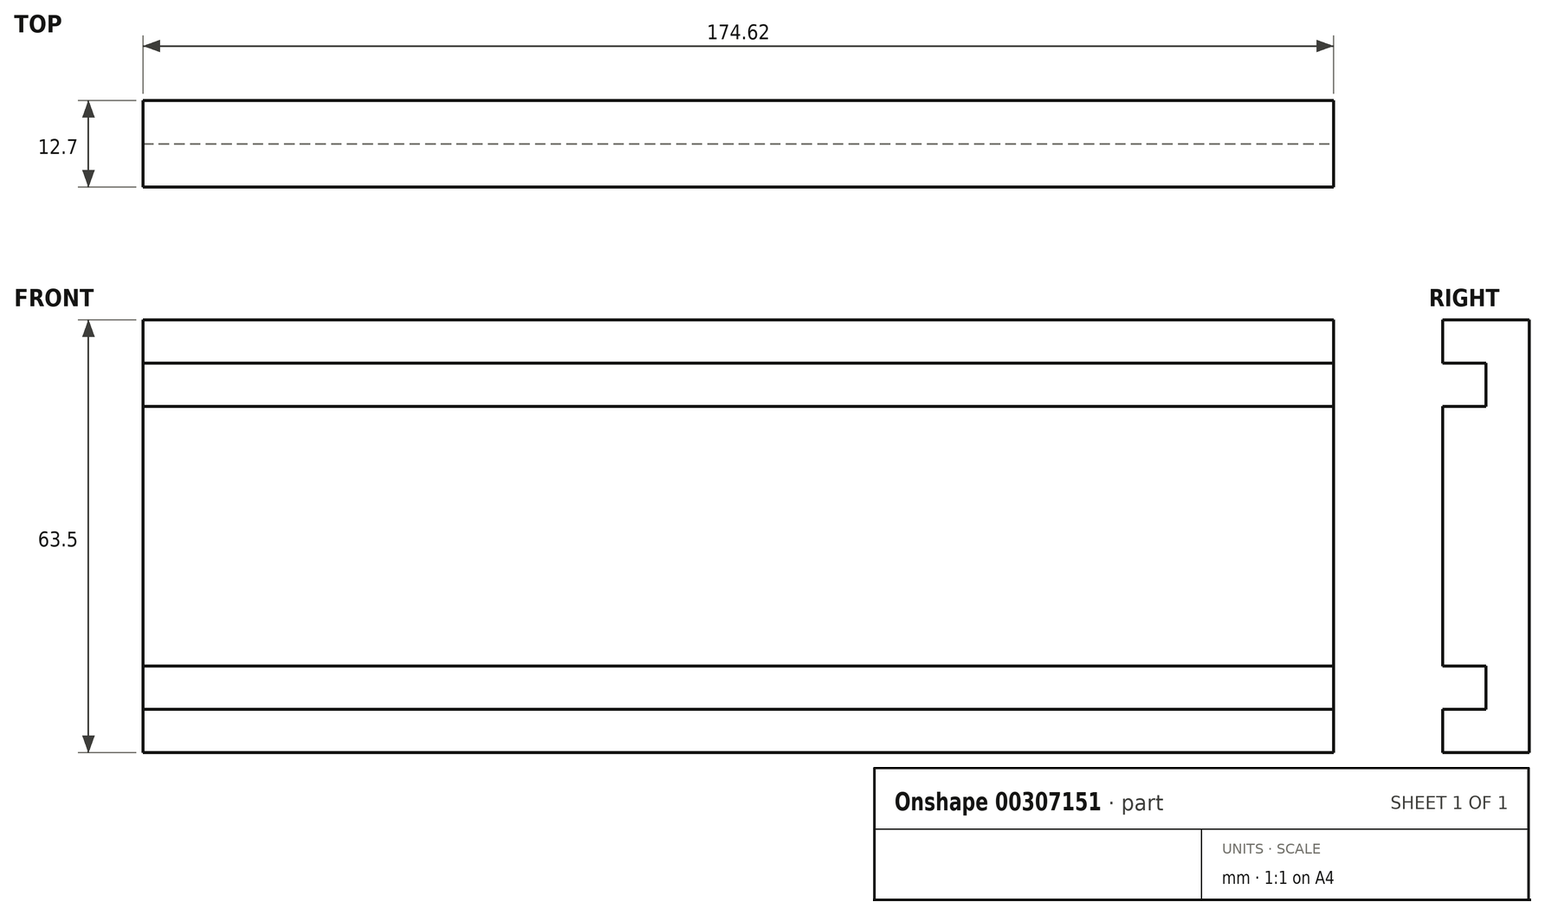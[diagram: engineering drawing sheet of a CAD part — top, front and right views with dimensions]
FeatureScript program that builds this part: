
annotation { "Feature Type Name" : "Feature", "Feature Type Description" : "" }
export const myFeature = defineFeature(function(context is Context, id is Id, definition is map)
    precondition{}
    {
        {
            var Q0;
            Q0=qCreatedBy(makeId("Front.planeOp"),FACE);
            var sketch = newSketch(context, id + "F0", { "sketchPlane" : qUnion([Q0])});
            skLineSegment(sketch, "E0.bottom", {"start": v(87.31, -31.75) * mm, "end": v(-87.31, -31.75) * mm});
            skLineSegment(sketch, "E0.top", {"start": v(87.31, 31.75) * mm, "end": v(-87.31, 31.75) * mm});
            skLineSegment(sketch, "E0.left", {"start": v(87.31, -31.75) * mm, "end": v(87.31, 31.75) * mm});
            skLineSegment(sketch, "E0.right", {"start": v(-87.31, -31.75) * mm, "end": v(-87.31, 31.75) * mm});
            skPoint(sketch, "E0.middle", {"position": v(0, 0) * mm});
            skSolve(sketch);
        }
        {
            var Q0;
            Q0=makeQuery(id+"F0.imprint","IMPRINT",FACE,{"disambiguationData":[TD([[makeQuery(id+"F0.imprint","IMPRINT",EDGE,{"derivedFrom":sQuery(id+"F0.wireOp",EDGE,"E0.bottom")}),-1.0]])]});
            extrude(context, id + "F1", {"entities" : qUnion([Q0]), "depth" : 12.7 * mm});
        }
        {
            var Q0;
            Q0=makeQuery(id+"F1.opExtrude","SWEPT_FACE",FACE,{"disambiguationData":[OSD([sQuery(id+"F0.wireOp",EDGE,"E0.left")])]});
            var sketch = newSketch(context, id + "F2", { "sketchPlane" : qUnion([Q0])});
            skLineSegment(sketch, "E1", {"start": v(-12.7, 25.4) * mm, "end": v(-6.35, 25.4) * mm});
            skLineSegment(sketch, "E2", {"start": v(-6.35, 25.4) * mm, "end": v(-6.35, 19.05) * mm});
            skLineSegment(sketch, "E3", {"start": v(-6.35, 19.05) * mm, "end": v(-12.7, 19.05) * mm});
            skLineSegment(sketch, "E4", {"start": v(-12.7, 19.05) * mm, "end": v(-12.7, -19.05) * mm});
            skLineSegment(sketch, "E5", {"start": v(-12.7, -19.05) * mm, "end": v(-6.35, -19.05) * mm});
            skLineSegment(sketch, "E6", {"start": v(-6.35, -19.05) * mm, "end": v(-6.35, -25.4) * mm});
            skLineSegment(sketch, "E7", {"start": v(-6.35, -25.4) * mm, "end": v(-12.7, -25.4) * mm});
            skSolve(sketch);
        }
        {
            var Q0;
            {var subQ0=sQuery(id+"F2.wireOp",EDGE,"E1");Q0=makeQuery(id+"F2.imprint","IMPRINT",FACE,{"disambiguationData":[TD([[makeQuery(id+"F2.imprint","IMPRINT",EDGE,{"derivedFrom":subQ0}),-1.0]])]});}
            var Q1;
            {var subQ0=sQuery(id+"F2.wireOp",EDGE,"E5");Q1=makeQuery(id+"F2.imprint","IMPRINT",FACE,{"disambiguationData":[TD([[makeQuery(id+"F2.imprint","IMPRINT",EDGE,{"derivedFrom":subQ0}),-1.0]])]});}
            var Q2;
            Q2=makeQuery(id+"F1.opExtrude","SWEPT_FACE",FACE,{"disambiguationData":[OSD([sQuery(id+"F0.wireOp",EDGE,"E0.right")])]});
            extrude(context, id + "F3", {"entities" : qUnion([Q0, Q1]), "operationType" : NewBodyOperationType.REMOVE, "endBound" : BoundingType.UP_TO_SURFACE, "oppositeDirection" : true, "endBoundEntityFace" : qUnion([Q2]), "depth" : 25.4 * mm});
        }
    });
